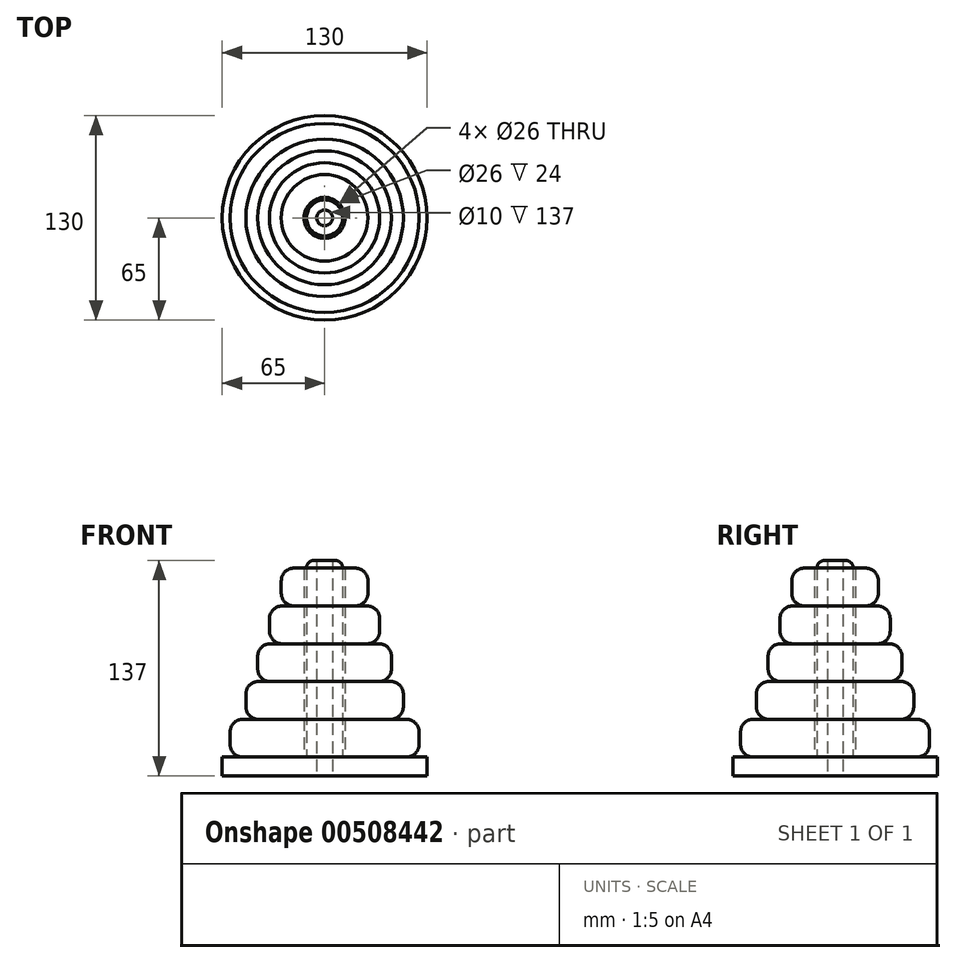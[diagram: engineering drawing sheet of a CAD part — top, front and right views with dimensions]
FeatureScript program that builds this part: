
annotation { "Feature Type Name" : "Feature", "Feature Type Description" : "" }
export const myFeature = defineFeature(function(context is Context, id is Id, definition is map)
    precondition{}
    {
        {
            var Q0;
            Q0=qCreatedBy(makeId("Top.planeOp"),FACE);
            var sketch = newSketch(context, id + "F0", { "sketchPlane" : qUnion([Q0])});
            skLineSegment(sketch, "E0.bottom", {"start": v(0, 0) * mm, "end": v(145, 0) * mm});
            skLineSegment(sketch, "E0.top", {"start": v(0, 145) * mm, "end": v(145, 145) * mm});
            skLineSegment(sketch, "E0.left", {"start": v(0, 0) * mm, "end": v(0, 145) * mm});
            skLineSegment(sketch, "E0.right", {"start": v(145, 0) * mm, "end": v(145, 145) * mm});
            skSolve(sketch);
        }
        {
            var Q0;
            Q0=makeQuery(id+"F0.imprint","IMPRINT",FACE,{"disambiguationData":[TD([[makeQuery(id+"F0.imprint","IMPRINT",EDGE,{"derivedFrom":sQuery(id+"F0.wireOp",EDGE,"E0.bottom")}),1.0]])]});
            extrude(context, id + "F1", {"entities" : qUnion([Q0]), "depth" : 12 * mm});
        }
        {
            var Q0;
            Q0=makeQuery(id+"F1.opExtrude","CAP_FACE",FACE,{"disambiguationData":[OSD([sQuery(id+"F0.wireOp",EDGE,"E0.bottom"),sQuery(id+"F0.wireOp",EDGE,"E0.top"),sQuery(id+"F0.wireOp",EDGE,"E0.left"),sQuery(id+"F0.wireOp",EDGE,"E0.right")])],"isStart":false});
            var sketch = newSketch(context, id + "F2", { "sketchPlane" : qUnion([Q0])});
            skLineSegment(sketch, "E1", {"start": v(0, 0) * mm, "end": v(72.5, 0) * mm});
            skCircle(sketch, "E2", {"center": v(72.5, 72.5) * mm, "radius": 11.5 * mm});
            skCircle(sketch, "E3", {"center": v(72.5, 72.5) * mm, "radius": 5 * mm});
            skSolve(sketch);
        }
        {
            var Q0;
            Q0=makeQuery(id+"F2.imprint","IMPRINT",FACE,{"disambiguationData":[TD([[makeQuery(id+"F2.imprint","IMPRINT",EDGE,{"derivedFrom":sQuery(id+"F2.wireOp",EDGE,"E2")}),1.0]])]});
            extrude(context, id + "F3", {"entities" : qUnion([Q0]), "operationType" : NewBodyOperationType.ADD, "depth" : 125 * mm});
        }
        {
            var Q0;
            {var subQ0=sQuery(id+"F0.wireOp",EDGE,"E0.left");var subQ1=sQuery(id+"F0.wireOp",EDGE,"E0.top");var subQ2=sQuery(id+"F0.wireOp",EDGE,"E0.right");var subQ3=sQuery(id+"F0.wireOp",EDGE,"E0.bottom");Q0=makeQuery(id+"F3.boolean.opBoolean","SPLIT",FACE,{"disambiguationData":[TD([makeQuery(id+"F1.opExtrude","SWEPT_FACE",FACE,{"disambiguationData":[OSD([subQ3])]})])],"derivedFrom":makeQuery(id+"F1.opExtrude","CAP_FACE",FACE,{"disambiguationData":[OSD([subQ3,subQ1,subQ0,subQ2])],"isStart":false})});}
            var sketch = newSketch(context, id + "F4", { "sketchPlane" : qUnion([Q0])});
            skCircle(sketch, "E4", {"center": v(72.5, 72.5) * mm, "radius": 60 * mm});
            skCircle(sketch, "E5", {"center": v(72.5, 72.5) * mm, "radius": 13 * mm});
            skSolve(sketch);
        }
        {
            var Q0;
            Q0=makeQuery(id+"F4.imprint","IMPRINT",FACE,{"disambiguationData":[TD([[makeQuery(id+"F4.imprint","IMPRINT",EDGE,{"derivedFrom":sQuery(id+"F4.wireOp",EDGE,"E4")}),1.0]])]});
            extrude(context, id + "F5", {"entities" : qUnion([Q0]), "depth" : 24 * mm});
        }
        {
            var Q0;
            Q0=makeQuery(id+"F5.opExtrude","CAP_FACE",FACE,{"disambiguationData":[OSD([sQuery(id+"F4.wireOp",EDGE,"E4"),sQuery(id+"F4.wireOp",EDGE,"E5")])],"isStart":false});
            var sketch = newSketch(context, id + "F6", { "sketchPlane" : qUnion([Q0])});
            skCircle(sketch, "E6", {"center": v(72.5, 72.5) * mm, "radius": 50 * mm});
            skCircle(sketch, "E7", {"center": v(72.5, 72.5) * mm, "radius": 13 * mm});
            skSolve(sketch);
        }
        {
            var Q0;
            Q0=makeQuery(id+"F6.imprint","IMPRINT",FACE,{"disambiguationData":[TD([[makeQuery(id+"F6.imprint","IMPRINT",EDGE,{"derivedFrom":sQuery(id+"F6.wireOp",EDGE,"E6")}),1.0]])]});
            extrude(context, id + "F7", {"entities" : qUnion([Q0]), "depth" : 24 * mm});
        }
        {
            var Q0;
            Q0=makeQuery(id+"F7.opExtrude","CAP_FACE",FACE,{"disambiguationData":[OSD([sQuery(id+"F6.wireOp",EDGE,"E6"),sQuery(id+"F6.wireOp",EDGE,"E7")])],"isStart":false});
            var sketch = newSketch(context, id + "F8", { "sketchPlane" : qUnion([Q0])});
            skCircle(sketch, "E8", {"center": v(72.5, 72.5) * mm, "radius": 42.5 * mm});
            skCircle(sketch, "E9", {"center": v(72.5, 72.5) * mm, "radius": 13 * mm});
            skSolve(sketch);
        }
        {
            var Q0;
            Q0=makeQuery(id+"F8.imprint","IMPRINT",FACE,{"disambiguationData":[TD([[makeQuery(id+"F8.imprint","IMPRINT",EDGE,{"derivedFrom":sQuery(id+"F8.wireOp",EDGE,"E8")}),1.0]])]});
            extrude(context, id + "F9", {"entities" : qUnion([Q0]), "depth" : 24 * mm});
        }
        {
            var Q0;
            Q0=makeQuery(id+"F9.opExtrude","CAP_FACE",FACE,{"disambiguationData":[OSD([sQuery(id+"F8.wireOp",EDGE,"E8"),sQuery(id+"F8.wireOp",EDGE,"E9")])],"isStart":false});
            var sketch = newSketch(context, id + "F10", { "sketchPlane" : qUnion([Q0])});
            skCircle(sketch, "E10", {"center": v(72.5, 72.5) * mm, "radius": 35 * mm});
            skCircle(sketch, "E11", {"center": v(72.5, 72.5) * mm, "radius": 13 * mm});
            skSolve(sketch);
        }
        {
            var Q0;
            Q0=makeQuery(id+"F10.imprint","IMPRINT",FACE,{"disambiguationData":[TD([[makeQuery(id+"F10.imprint","IMPRINT",EDGE,{"derivedFrom":sQuery(id+"F10.wireOp",EDGE,"E10")}),1.0]])]});
            extrude(context, id + "F11", {"entities" : qUnion([Q0]), "depth" : 24 * mm});
        }
        {
            var Q0;
            Q0=makeQuery(id+"F11.opExtrude","CAP_FACE",FACE,{"disambiguationData":[OSD([sQuery(id+"F10.wireOp",EDGE,"E10"),sQuery(id+"F10.wireOp",EDGE,"E11")])],"isStart":false});
            var sketch = newSketch(context, id + "F12", { "sketchPlane" : qUnion([Q0])});
            skCircle(sketch, "E12", {"center": v(72.5, 72.5) * mm, "radius": 27.5 * mm});
            skCircle(sketch, "E13", {"center": v(72.5, 72.5) * mm, "radius": 13 * mm});
            skSolve(sketch);
        }
        {
            var Q0;
            Q0=makeQuery(id+"F12.imprint","IMPRINT",FACE,{"disambiguationData":[TD([[makeQuery(id+"F12.imprint","IMPRINT",EDGE,{"derivedFrom":sQuery(id+"F12.wireOp",EDGE,"E12")}),1.0]])]});
            extrude(context, id + "F13", {"entities" : qUnion([Q0]), "depth" : 24 * mm});
        }
        {
            var Q0;
            Q0=makeQuery(id+"F13.opExtrude","SWEPT_FACE",FACE,{"disambiguationData":[OSD([sQuery(id+"F12.wireOp",EDGE,"E12")])]});
            fillet(context, id + "F14", {"entities" : qUnion([Q0]), "radius" : 8 * mm, "tangentPropagation" : true, "allowEdgeOverflow" : false});
        }
        {
            var Q0;
            Q0=makeQuery(id+"F11.opExtrude","SWEPT_FACE",FACE,{"disambiguationData":[OSD([sQuery(id+"F10.wireOp",EDGE,"E10")])]});
            fillet(context, id + "F15", {"entities" : qUnion([Q0]), "radius" : 8 * mm, "tangentPropagation" : true, "allowEdgeOverflow" : false});
        }
        {
            var Q0;
            Q0=makeQuery(id+"F9.opExtrude","SWEPT_FACE",FACE,{"disambiguationData":[OSD([sQuery(id+"F8.wireOp",EDGE,"E8")])]});
            fillet(context, id + "F16", {"entities" : qUnion([Q0]), "radius" : 8 * mm, "tangentPropagation" : true, "allowEdgeOverflow" : false});
        }
        {
            var Q0;
            Q0=makeQuery(id+"F7.opExtrude","SWEPT_FACE",FACE,{"disambiguationData":[OSD([sQuery(id+"F6.wireOp",EDGE,"E6")])]});
            fillet(context, id + "F17", {"entities" : qUnion([Q0]), "radius" : 8 * mm, "tangentPropagation" : true, "allowEdgeOverflow" : false});
        }
        {
            var Q0;
            Q0=makeQuery(id+"F5.opExtrude","SWEPT_FACE",FACE,{"disambiguationData":[OSD([sQuery(id+"F4.wireOp",EDGE,"E4")])]});
            fillet(context, id + "F18", {"entities" : qUnion([Q0]), "radius" : 8 * mm, "tangentPropagation" : true, "allowEdgeOverflow" : false});
        }
        {
            var Q0;
            Q0=makeQuery(id+"F3.opExtrude","CAP_EDGE",EDGE,{"disambiguationData":[OSD([sQuery(id+"F2.wireOp",EDGE,"E2")])],"isStart":false});
            fillet(context, id + "F19", {"entities" : qUnion([Q0]), "radius" : 5 * mm, "tangentPropagation" : true, "allowEdgeOverflow" : false});
        }
        {
            var Q0;
            {var subQ0=sQuery(id+"F0.wireOp",EDGE,"E0.left");var subQ1=sQuery(id+"F0.wireOp",EDGE,"E0.top");var subQ2=sQuery(id+"F0.wireOp",EDGE,"E0.right");var subQ3=sQuery(id+"F0.wireOp",EDGE,"E0.bottom");Q0=makeQuery(id+"F3.boolean.opBoolean","SPLIT",FACE,{"disambiguationData":[TD([makeQuery(id+"F1.opExtrude","SWEPT_FACE",FACE,{"disambiguationData":[OSD([subQ3])]})])],"derivedFrom":makeQuery(id+"F1.opExtrude","CAP_FACE",FACE,{"disambiguationData":[OSD([subQ3,subQ1,subQ0,subQ2])],"isStart":false})});}
            var sketch = newSketch(context, id + "F20", { "sketchPlane" : qUnion([Q0])});
            skCircle(sketch, "E14", {"center": v(72.5, 72.5) * mm, "radius": 5 * mm});
            skSolve(sketch);
        }
        {
            var Q0;
            Q0=sQuery(id+"F20.wireOp",VERTEX,"E14.center");
            var Q1;
            Q1=makeQuery(id+"F1.opExtrude","SWEPT_BODY",BODY,{"disambiguationData":[OSD([sQuery(id+"F0.wireOp",EDGE,"E0.bottom"),sQuery(id+"F0.wireOp",EDGE,"E0.top"),sQuery(id+"F0.wireOp",EDGE,"E0.left"),sQuery(id+"F0.wireOp",EDGE,"E0.right")])]});
            hole(context, id + "F21", {"style" : HoleStyle.SIMPLE, "endStyle" : HoleEndStyle.THROUGH, "holeDiameter" : 10 * mm, "isTappedThrough" : true, "tappedDepth" : 12 * mm, "tapClearance" : 3, "locations" : qUnion([Q0]), "scope" : qUnion([Q1])});
        }
        {
            var Q0;
            {var subQ0=sQuery(id+"F0.wireOp",EDGE,"E0.left");var subQ1=sQuery(id+"F0.wireOp",EDGE,"E0.top");var subQ2=sQuery(id+"F0.wireOp",EDGE,"E0.right");var subQ3=sQuery(id+"F0.wireOp",EDGE,"E0.bottom");Q0=makeQuery(id+"F3.boolean.opBoolean","SPLIT",FACE,{"disambiguationData":[TD([makeQuery(id+"F1.opExtrude","SWEPT_FACE",FACE,{"disambiguationData":[OSD([subQ3])]})])],"derivedFrom":makeQuery(id+"F1.opExtrude","CAP_FACE",FACE,{"disambiguationData":[OSD([subQ3,subQ1,subQ0,subQ2])],"isStart":false})});}
            var sketch = newSketch(context, id + "F22", { "sketchPlane" : qUnion([Q0])});
            skCircle(sketch, "E15", {"center": v(72.5, 72.5) * mm, "radius": 65 * mm});
            skSolve(sketch);
        }
        {
            var Q0;
            Q0=makeQuery(id+"F22.imprint","IMPRINT",FACE,{"disambiguationData":[TD([[makeQuery(id+"F22.imprint","IMPRINT",EDGE,{"derivedFrom":sQuery(id+"F22.wireOp",EDGE,"E15")}),-1.0]])]});
            extrude(context, id + "F23", {"entities" : qUnion([Q0]), "operationType" : NewBodyOperationType.REMOVE, "endBound" : BoundingType.UP_TO_NEXT, "oppositeDirection" : true, "depth" : 25 * mm});
        }
    });
